# Revit family: SP1
name_source: partatom
category: Lighting Fixtures
units: mm (PartAtom-declared; Revit-internal decimal feet)

## family parameters
Always vertical = Yes
Cut with Voids When Loaded = No
Light Source = Yes
Part Type = Normal
Room Calculation Point = No
Round Connector Dimension = Use Diameter
Shared = No
Work Plane-Based = No

## types (1)
- 31.5" , SP1-STR-GR5-100PSMH
    AAL IES File = SP1-STR-GR5-100PSMH.IES
    Absolute Lumens = 9000 lm
    Apparent Load = 57 VA
    Assembly Code = D5020210
    Color Filter = 16777215
    Default Elevation = 0' - 0"
    Default elevation = 0' - 0"
    Description = Exterior Lighting
    Dimming Lamp Color Temperature Shift = <None>
    Frequency = 60 Hz
    Full Load Current = 1 A
    GLA = No
    GR = Yes
    Glazing Type = Glass-Acrylic
    Height = 2' - 5"
    Hood Height = 0' - 6 1/2"
    Housing Material = Aluminum-Artic White
    LDL = No
    Lamp = 100 WATT CLEAR VERTICAL  BASE DOWN PSMH ED17/E26
    Lens Type = 2
    Manufacturer = Architectural Area Lighting
    MasterFormat Number = 26.56.29
    MasterFormat Title = Area Lighting
    Model = SP1-STR-GR5-100PSMH
    Note Text = LF
    Note Visible = Yes
    Number of Poles = 1
    OmniClass Number = 23.80.70.14.11.14
    OmniClass Title = Post-Top Lighting
    Photometric Web File = generic.ies
    Power Factor = 1
    Series = Spectra
    Support Material = Aluminum-Grey Satin
    Tilt Angle = 90.00°
    URL = https://www.currentlighting.com
    Voltage = 277 V
    Wattage Comments = MH 100W/U/PS VENTURE
    Width = 2' - 7 1/2"
    Width Radius = 1' - 3 3/4"

## geometry (parser evidence)
native form markers: Sweep x4
no freeform markers — native parametric forms only
